# Revit family: Shower_Base-American_Standard-38x38-A8009D-FCO
name_source: partatom
category: Plumbing Fixtures
revit_build: Autodesk Revit 2014 (Build: 20130308_1515(x64)
units: mm (PartAtom-declared; Revit-internal decimal feet)

## types (1)
- A8009D-FCO
    ADA Compliant = Yes
    Assembly Code = D2010710
    CW Connection = No
    CWFU = 3
    Clearance Between Studding = 0"
    Default Elevation = 0"
    Description = 38" x 38" Shower Base
    Drain Length = 18 1/2"
    Drain Location = 19"
    Finish = Acrylic-American Standard-001-White
    HW Connection = No
    HWFU = 3
    Height = 2 1/8"
    Installation Type = Floor Mounted
    Length = 38"
    Manufacturer = American Standard
    Material = Acrylic-American Standard-001-White
    Model = A8009D-FCO
    Price = Prices may vary. Please consult Manufacturer Representative for most up-to-date price list.
    Strainer Finish = Stainless Steel-American Standard-Satin
    URL = https://www.americanstandard-us.com
    Vent Connection = No
    WFU = 4
    Warranty Information = Limited Lifetime Warranty
    Waste Connection = Yes
    Waste Connection Diameter = 3 1/4"
    Waste Connection Radius = 1 5/8"
    Width = 38"

## geometry (parser evidence)
native form markers: Sweep x1
no freeform markers — native parametric forms only
